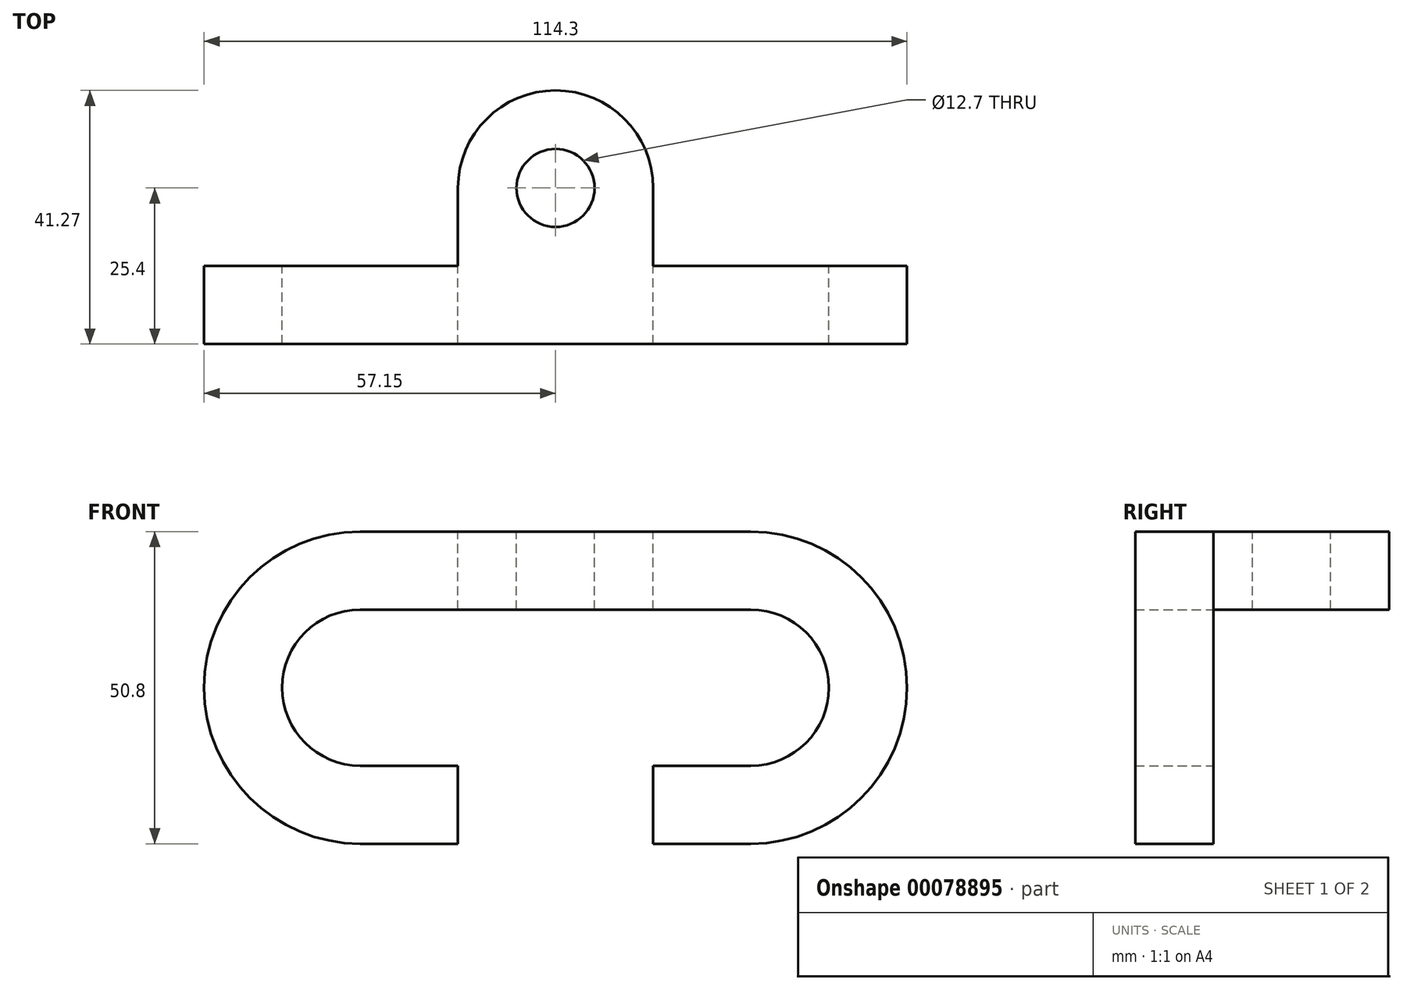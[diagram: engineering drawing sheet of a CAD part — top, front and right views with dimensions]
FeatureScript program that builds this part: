
annotation { "Feature Type Name" : "Feature", "Feature Type Description" : "" }
export const myFeature = defineFeature(function(context is Context, id is Id, definition is map)
    precondition{}
    {
        {
            var Q0;
            Q0=qCreatedBy(makeId("Front.planeOp"),FACE);
            var sketch = newSketch(context, id + "F0", { "sketchPlane" : qUnion([Q0])});
            skLineSegment(sketch, "E0.bottom", {"start": v(0, 0) * mm, "end": v(31.75, 0) * mm});
            skLineSegment(sketch, "E0.top", {"start": v(0, -12.7) * mm, "end": v(31.75, -12.7) * mm});
            skLineSegment(sketch, "E0.left", {"start": v(0, 0) * mm, "end": v(0, -12.7) * mm});
            skArc(sketch, "E1", {"start": v(31.75, -50.8) * mm, "mid": v(57.15, -25.4) * mm, "end": v(31.75, 0) * mm});
            skArc(sketch, "E2", {"start": v(31.75, -38.1) * mm, "mid": v(44.45, -25.4) * mm, "end": v(31.75, -12.7) * mm});
            skLineSegment(sketch, "E3.bottom", {"start": v(31.75, -50.8) * mm, "end": v(15.88, -50.8) * mm});
            skLineSegment(sketch, "E3.top", {"start": v(31.75, -38.1) * mm, "end": v(15.88, -38.1) * mm});
            skLineSegment(sketch, "E3.right", {"start": v(15.88, -50.8) * mm, "end": v(15.88, -38.1) * mm});
            skSolve(sketch);
        }
        {
            var Q0;
            Q0 = qSketchRegion(id + "F0", true);
            extrude(context, id + "F1", {"entities" : qUnion([Q0]), "depth" : 12.7 * mm});
        }
        {
            var Q0;
            {var subQ0=makeQuery(id+"F1.opExtrude","SWEPT_FACE",FACE,{"disambiguationData":[OSD([sQuery(id+"F0.wireOp",EDGE,"E0.bottom")])]});Q0=makeQuery(id+"F4.boolean.opBoolean","MERGE",FACE,{"derivedFrom":[subQ0,makeQuery(id+"F4.opPattern","COPY",FACE,{"derivedFrom":subQ0,"instanceName":"1"})]});}
            var sketch = newSketch(context, id + "F2", { "sketchPlane" : qUnion([Q0])});
            skArc(sketch, "E4", {"start": v(15.88, 12.7) * mm, "mid": v(11.23, 23.93) * mm, "end": v(0, 28.58) * mm});
            skArc(sketch, "E5", {"start": v(0, 6.35) * mm, "mid": v(6.35, 12.7) * mm, "end": v(0, 19.05) * mm});
            skLineSegment(sketch, "E6", {"start": v(0, 28.58) * mm, "end": v(0, 0) * mm});
            skLineSegment(sketch, "E7", {"start": v(15.88, 12.7) * mm, "end": v(15.88, 0) * mm});
            skSolve(sketch);
        }
        {
            var Q0;
            {var subQ6=sQuery(id+"F2.wireOp",EDGE,"E4");Q0=makeQuery(id+"F2.imprint","IMPRINT",FACE,{"disambiguationData":[TD([[makeQuery(id+"F2.imprint","IMPRINT",EDGE,{"derivedFrom":subQ6}),1.0]])]});}
            var Q1;
            Q1=makeQuery(id+"F1.opExtrude","SWEPT_FACE",FACE,{"disambiguationData":[OSD([sQuery(id+"F0.wireOp",EDGE,"E0.top")])]});
            extrude(context, id + "F3", {"entities" : qUnion([Q0]), "operationType" : NewBodyOperationType.ADD, "endBound" : BoundingType.UP_TO_SURFACE, "oppositeDirection" : true, "endBoundEntityFace" : qUnion([Q1]), "depth" : 25.4 * mm});
        }
        {
            var Q0;
            Q0=makeQuery(id+"F1.opExtrude","SWEPT_BODY",BODY,{"disambiguationData":[OSD([sQuery(id+"F0.wireOp",EDGE,"E0.bottom"),sQuery(id+"F0.wireOp",EDGE,"E0.top"),sQuery(id+"F0.wireOp",EDGE,"E0.left"),sQuery(id+"F0.wireOp",EDGE,"E1"),sQuery(id+"F0.wireOp",EDGE,"E2"),sQuery(id+"F0.wireOp",EDGE,"E3.bottom"),sQuery(id+"F0.wireOp",EDGE,"E3.top"),sQuery(id+"F0.wireOp",EDGE,"E3.right")])]});
            var Q1;
            Q1=makeQuery(id+"F1.opExtrude","SWEPT_FACE",FACE,{"disambiguationData":[OSD([sQuery(id+"F0.wireOp",EDGE,"E0.left")])]});
            mirror(context, id + "F4", {"operationType" : NewBodyOperationType.ADD, "entities" : qUnion([Q0]), "mirrorPlane" : qUnion([Q1])});
        }
    });
